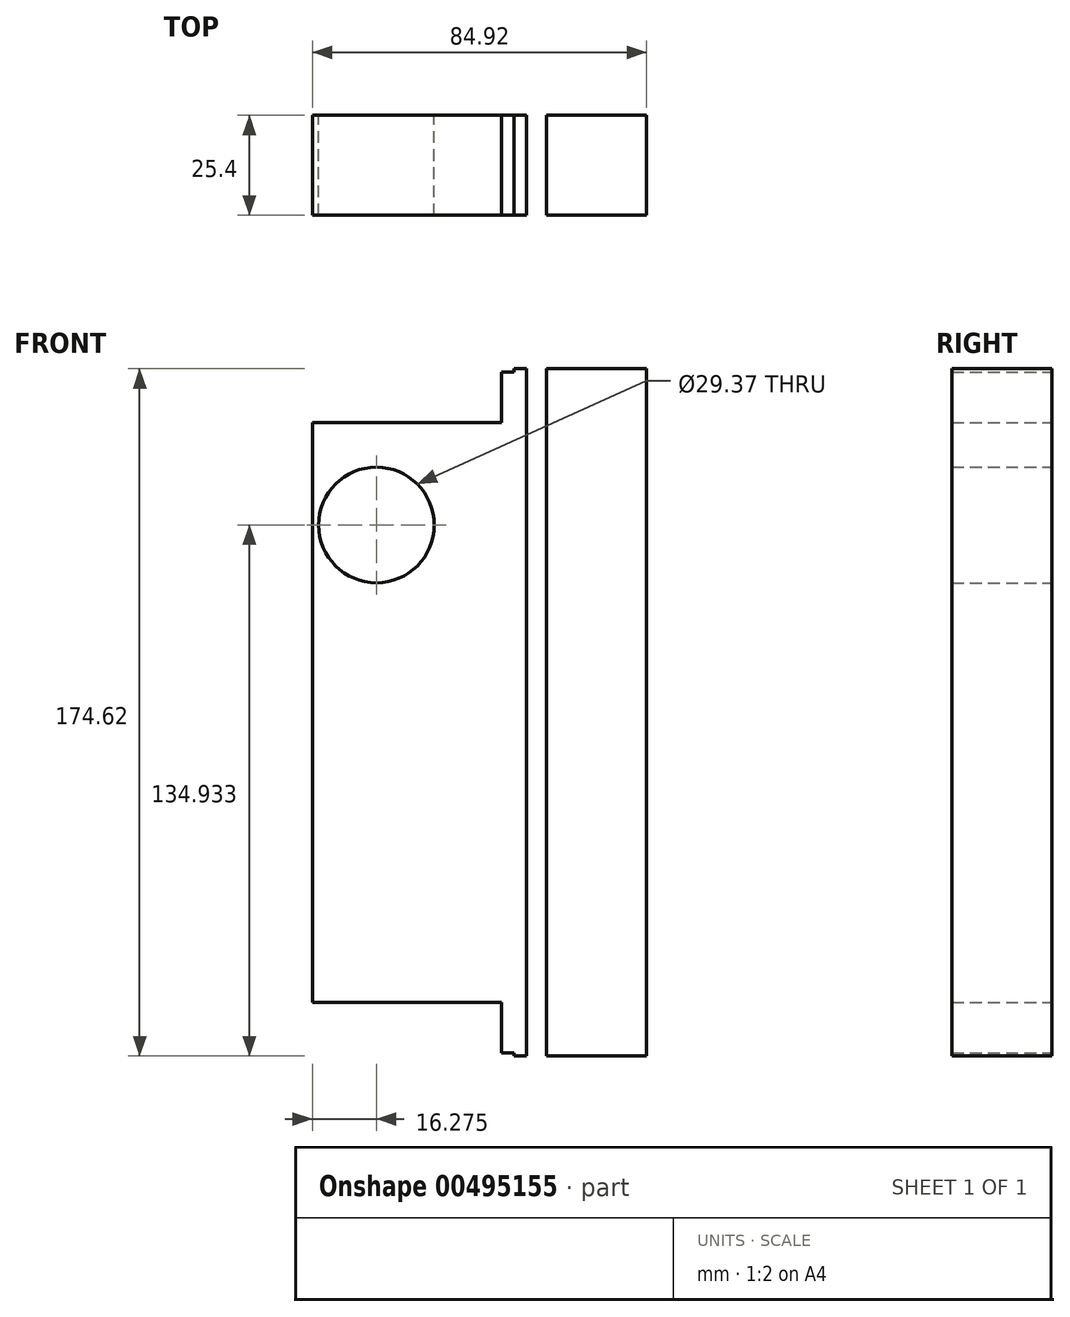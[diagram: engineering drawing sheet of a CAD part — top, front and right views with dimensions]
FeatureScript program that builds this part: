
annotation { "Feature Type Name" : "Feature", "Feature Type Description" : "" }
export const myFeature = defineFeature(function(context is Context, id is Id, definition is map)
    precondition{}
    {
        {
            var Q0;
            Q0=qCreatedBy(makeId("Front.planeOp"),FACE);
            var sketch = newSketch(context, id + "F0", { "sketchPlane" : qUnion([Q0])});
            skLineSegment(sketch, "E0", {"start": v(-26.64, 62.5) * mm, "end": v(21.39, 62.5) * mm});
            skLineSegment(sketch, "E1", {"start": v(21.39, 62.5) * mm, "end": v(21.39, 75.4) * mm});
            skLineSegment(sketch, "E2", {"start": v(21.39, 75.4) * mm, "end": v(24.56, 75.4) * mm});
            skLineSegment(sketch, "E3", {"start": v(24.56, 75.4) * mm, "end": v(24.56, 76.2) * mm});
            skLineSegment(sketch, "E4", {"start": v(24.56, 76.2) * mm, "end": v(27.74, 76.2) * mm});
            skLineSegment(sketch, "E5", {"start": v(27.74, 76.2) * mm, "end": v(27.74, -98.42) * mm});
            skLineSegment(sketch, "E6", {"start": v(27.74, -98.42) * mm, "end": v(24.56, -98.42) * mm});
            skLineSegment(sketch, "E7", {"start": v(24.56, -98.42) * mm, "end": v(24.56, -97.63) * mm});
            skLineSegment(sketch, "E8", {"start": v(24.56, -97.63) * mm, "end": v(21.39, -97.63) * mm});
            skLineSegment(sketch, "E9", {"start": v(21.39, -97.63) * mm, "end": v(21.39, -84.73) * mm});
            skLineSegment(sketch, "E10", {"start": v(21.39, -84.73) * mm, "end": v(-26.64, -84.73) * mm});
            skLineSegment(sketch, "E11", {"start": v(-26.64, -84.73) * mm, "end": v(-26.64, 62.5) * mm});
            skCircle(sketch, "E12", {"center": v(-10.36, 36.51) * mm, "radius": 14.68 * mm});
            skLineSegment(sketch, "E13.bottom", {"start": v(32.88, 76.2) * mm, "end": v(58.28, 76.2) * mm});
            skLineSegment(sketch, "E13.top", {"start": v(32.88, -98.42) * mm, "end": v(58.28, -98.42) * mm});
            skLineSegment(sketch, "E13.left", {"start": v(32.88, 76.2) * mm, "end": v(32.88, -98.42) * mm});
            skLineSegment(sketch, "E13.right", {"start": v(58.28, 76.2) * mm, "end": v(58.28, -98.42) * mm});
            skSolve(sketch);
        }
        {
            var Q0;
            Q0=makeQuery(id+"F0.imprint","IMPRINT",FACE,{"disambiguationData":[TD([[makeQuery(id+"F0.imprint","IMPRINT",EDGE,{"derivedFrom":sQuery(id+"F0.wireOp",EDGE,"E0")}),-1.0]])]});
            var Q1;
            Q1=makeQuery(id+"F0.imprint","IMPRINT",FACE,{"disambiguationData":[TD([[makeQuery(id+"F0.imprint","IMPRINT",EDGE,{"derivedFrom":sQuery(id+"F0.wireOp",EDGE,"E13.bottom")}),-1.0]])]});
            extrude(context, id + "F1", {"entities" : qUnion([Q0, Q1]), "depth" : 25.4 * mm});
        }
    });
